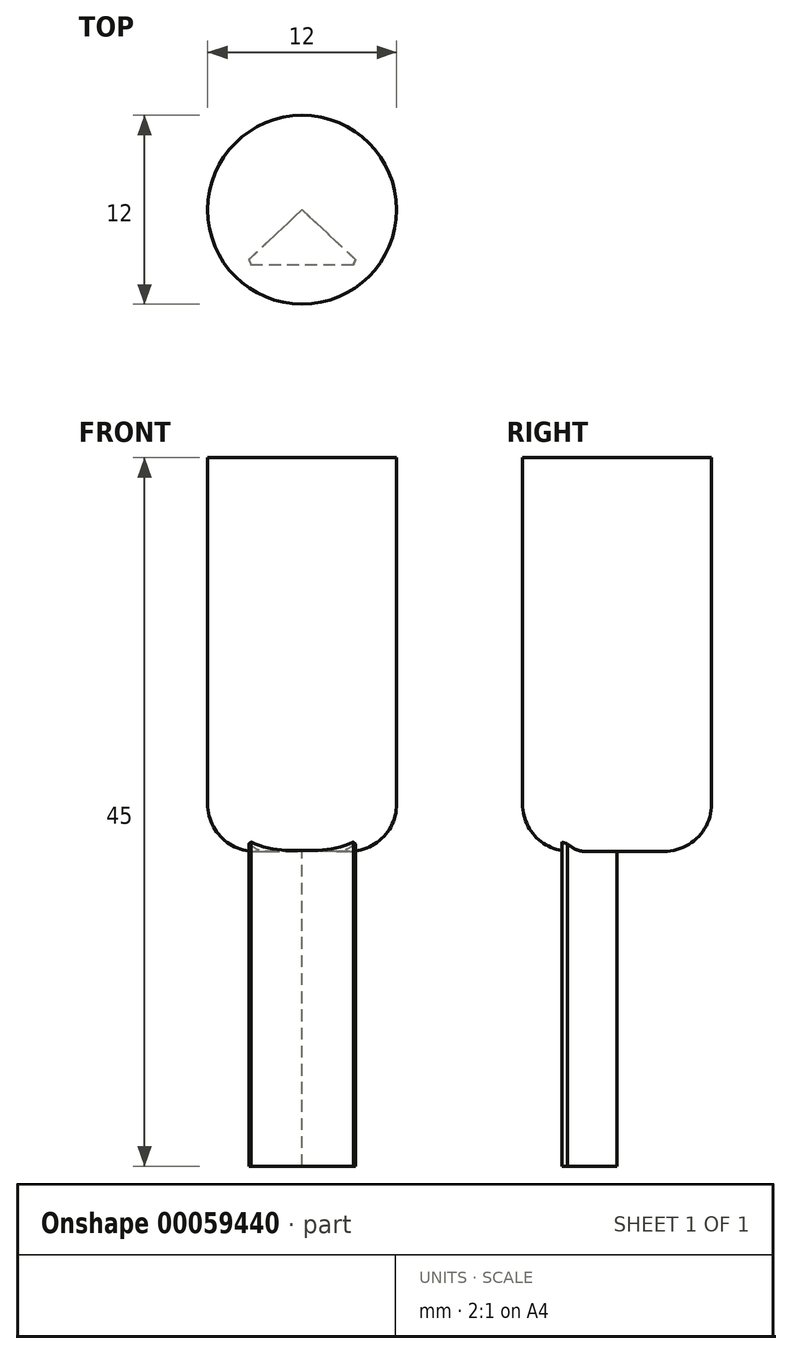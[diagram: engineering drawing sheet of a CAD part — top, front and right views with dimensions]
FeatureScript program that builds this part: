
annotation { "Feature Type Name" : "Feature", "Feature Type Description" : "" }
export const myFeature = defineFeature(function(context is Context, id is Id, definition is map)
    precondition{}
    {
        {
            var Q0;
            Q0=qCreatedBy(makeId("Top.planeOp"),FACE);
            var sketch = newSketch(context, id + "F0", { "sketchPlane" : qUnion([Q0])});
            skLineSegment(sketch, "E0", {"start": v(0, 0) * mm, "end": v(-7.5, 0) * mm});
            skLineSegment(sketch, "E1", {"start": v(-7.5, 0) * mm, "end": v(-3.75, 0) * mm});
            skLineSegment(sketch, "E2", {"start": v(-3.75, 0) * mm, "end": v(-3.75, 3.5) * mm});
            skLineSegment(sketch, "E3", {"start": v(-7.5, 0) * mm, "end": v(-3.75, 3.5) * mm});
            skLineSegment(sketch, "E4", {"start": v(0, 0) * mm, "end": v(-3.75, 3.5) * mm});
            skCircle(sketch, "E5", {"center": v(-3.75, 3.5) * mm, "radius": 6 * mm});
            skSolve(sketch);
        }
        {
            var Q0;
            Q0=makeQuery(id+"F0.imprint","IMPRINT",FACE,{"disambiguationData":[TD([[makeQuery(id+"F0.imprint","IMPRINT",EDGE,{"derivedFrom":sQuery(id+"F0.wireOp",EDGE,"E0")}),-1.0]])]});
            var Q1;
            Q1=makeQuery(id+"F0.imprint","IMPRINT",FACE,{"disambiguationData":[TD([[makeQuery(id+"F0.imprint","IMPRINT",EDGE,{"derivedFrom":sQuery(id+"F0.wireOp",EDGE,"E1")}),1.0]])]});
            extrude(context, id + "F1", {"entities" : qUnion([Q0, Q1]), "oppositeDirection" : true, "depth" : 20 * mm, "offsetDistance" : 25 * mm});
        }
        {
            var Q0;
            Q0 = qSketchRegion(id + "F0", true);
            var Q1;
            Q1=makeQuery(id+"F1.opExtrude","CAP_FACE",FACE,{"disambiguationData":[OSD([sQuery(id+"F0.wireOp",EDGE,"E0"),sQuery(id+"F0.wireOp",EDGE,"E1"),sQuery(id+"F0.wireOp",EDGE,"E3"),sQuery(id+"F0.wireOp",EDGE,"E4")])],"isStart":true});
            extrude(context, id + "F2", {"entities" : qUnion([Q0, Q1]), "operationType" : NewBodyOperationType.ADD, "depth" : 25 * mm, "offsetDistance" : 25 * mm});
        }
        {
            var Q0;
            Q0=makeQuery(id+"F2.opExtrude","CAP_EDGE",EDGE,{"disambiguationData":[OSD([sQuery(id+"F0.wireOp",EDGE,"E5")])],"isStart":true});
            fillet(context, id + "F3", {"entities" : qUnion([Q0]), "radius" : 3 * mm, "tangentPropagation" : true, "allowEdgeOverflow" : false});
        }
        {
            var Q0;
            Q0=makeQuery(id+"F1.opExtrude","SWEPT_EDGE",EDGE,{"disambiguationData":[OSD([sQuery(id+"F0.wireOp",EDGE,"E1"),sQuery(id+"F0.wireOp",EDGE,"E3")])]});
            var Q1;
            Q1=makeQuery(id+"F1.opExtrude","SWEPT_EDGE",EDGE,{"disambiguationData":[OSD([sQuery(id+"F0.wireOp",EDGE,"E0"),sQuery(id+"F0.wireOp",EDGE,"E4")])]});
            chamfer(context, id + "F4", {"entities" : qUnion([Q0, Q1]), "width" : .5 * mm, "tangentPropagation" : true});
        }
    });
